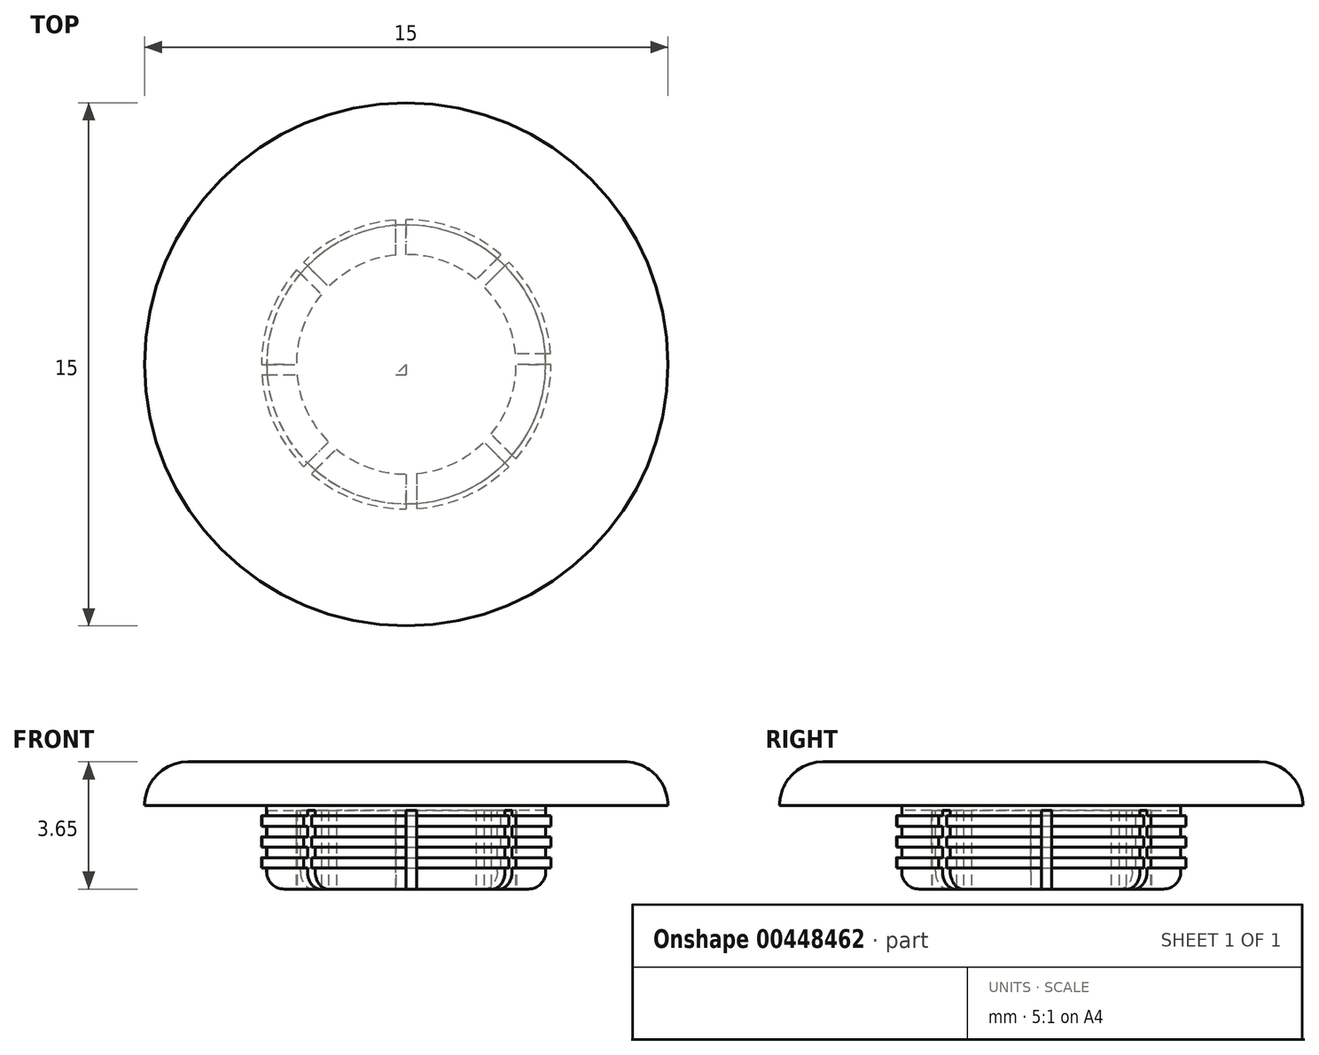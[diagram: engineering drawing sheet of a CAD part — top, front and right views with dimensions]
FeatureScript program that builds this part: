
annotation { "Feature Type Name" : "Feature", "Feature Type Description" : "" }
export const myFeature = defineFeature(function(context is Context, id is Id, definition is map)
    precondition{}
    {
        {
            var Q0;
            Q0=qCreatedBy(makeId("Top.planeOp"),FACE);
            var sketch = newSketch(context, id + "F0", { "sketchPlane" : qUnion([Q0])});
            skCircle(sketch, "E0", {"center": v(0, 0) * mm, "radius": 7.5 * mm});
            skCircle(sketch, "E1", {"center": v(0, 0) * mm, "radius": 4 * mm});
            skCircle(sketch, "E2", {"center": v(0, 0) * mm, "radius": 3.15 * mm});
            skSolve(sketch);
        }
        {
            var Q0;
            Q0=makeQuery(id+"F0.imprint","IMPRINT",FACE,{"disambiguationData":[TD([[makeQuery(id+"F0.imprint","IMPRINT",EDGE,{"derivedFrom":sQuery(id+"F0.wireOp",EDGE,"E0")}),1.0]])]});
            var Q1;
            Q1=makeQuery(id+"F0.imprint","IMPRINT",FACE,{"disambiguationData":[TD([[makeQuery(id+"F0.imprint","IMPRINT",EDGE,{"derivedFrom":sQuery(id+"F0.wireOp",EDGE,"E1")}),1.0]])]});
            var Q2;
            Q2=makeQuery(id+"F0.imprint","IMPRINT",FACE,{"disambiguationData":[TD([[makeQuery(id+"F0.imprint","IMPRINT",EDGE,{"derivedFrom":sQuery(id+"F0.wireOp",EDGE,"E2")}),1.0]])]});
            extrude(context, id + "F1", {"entities" : qUnion([Q0, Q1, Q2]), "depth" : 1.25 * mm});
        }
        {
            var Q0;
            Q0=makeQuery(id+"F1.opExtrude","CAP_EDGE",EDGE,{"disambiguationData":[OSD([sQuery(id+"F0.wireOp",EDGE,"E0")])],"isStart":false});
            fillet(context, id + "F2", {"entities" : qUnion([Q0]), "radius" : 1.25 * mm, "tangentPropagation" : true, "allowEdgeOverflow" : false});
        }
        {
            var Q0;
            Q0=makeQuery(id+"F0.imprint","IMPRINT",FACE,{"disambiguationData":[TD([[makeQuery(id+"F0.imprint","IMPRINT",EDGE,{"derivedFrom":sQuery(id+"F0.wireOp",EDGE,"E1")}),1.0]])]});
            var Q1;
            Q1=makeQuery(id+"F0.imprint","IMPRINT",FACE,{"disambiguationData":[TD([[makeQuery(id+"F0.imprint","IMPRINT",EDGE,{"derivedFrom":sQuery(id+"F0.wireOp",EDGE,"E2")}),1.0]])]});
            extrude(context, id + "F3", {"entities" : qUnion([Q0, Q1]), "operationType" : NewBodyOperationType.ADD, "oppositeDirection" : true, "depth" : .3 * mm});
        }
        {
            var Q0;
            Q0=makeQuery(id+"F3.opExtrude","CAP_FACE",FACE,{"disambiguationData":[OSD([sQuery(id+"F0.wireOp",EDGE,"E1"),sQuery(id+"F0.wireOp",EDGE,"E2")])],"isStart":false});
            var sketch = newSketch(context, id + "F4", { "sketchPlane" : qUnion([Q0])});
            skCircle(sketch, "E3", {"center": v(0, 0) * mm, "radius": 4.15 * mm});
            skSolve(sketch);
        }
        {
            var Q0;
            Q0=makeQuery(id+"F4.imprint","IMPRINT",FACE,{"disambiguationData":[TD([[makeQuery(id+"F4.imprint","IMPRINT",EDGE,{"derivedFrom":sQuery(id+"F4.wireOp",EDGE,"E3")}),1.0]])]});
            var Q1;
            Q1=makeQuery(id+"F4.imprint","IMPRINT",FACE,{"disambiguationData":[TD([[makeQuery(id+"F4.imprint","IMPRINT",EDGE,{"derivedFrom":makeQuery(id+"F3.opExtrude","CAP_EDGE",EDGE,{"disambiguationData":[OSD([sQuery(id+"F0.wireOp",EDGE,"E1")])],"isStart":false})}),-1.0]])]});
            var Q2;
            Q2=makeQuery(id+"F4.imprint","IMPRINT",FACE,{"disambiguationData":[TD([[makeQuery(id+"F4.imprint","IMPRINT",EDGE,{"derivedFrom":makeQuery(id+"F3.opExtrude","CAP_EDGE",EDGE,{"disambiguationData":[OSD([sQuery(id+"F0.wireOp",EDGE,"E2")])],"isStart":false})}),-1.0]])]});
            extrude(context, id + "F5", {"entities" : qUnion([Q0, Q1, Q2]), "operationType" : NewBodyOperationType.ADD, "depth" : .3 * mm});
        }
        {
            var Q0;
            Q0=makeQuery(id+"F5.opExtrude","CAP_FACE",FACE,{"disambiguationData":[OSD([sQuery(id+"F4.wireOp",EDGE,"E3")])],"isStart":false});
            var sketch = newSketch(context, id + "F6", { "sketchPlane" : qUnion([Q0])});
            skCircle(sketch, "E4", {"center": v(0, 0) * mm, "radius": 4 * mm});
            skSolve(sketch);
        }
        {
            var Q0;
            Q0=qSketchRegion(id+"F6",true);
            extrude(context, id + "F7", {"entities" : qUnion([Q0]), "operationType" : NewBodyOperationType.ADD, "depth" : .3 * mm});
        }
        {
            var Q0;
            Q0=makeQuery(id+"F7.opExtrude","CAP_FACE",FACE,{"disambiguationData":[OSD([sQuery(id+"F6.wireOp",EDGE,"E4")])],"isStart":false});
            var sketch = newSketch(context, id + "F8", { "sketchPlane" : qUnion([Q0])});
            skCircle(sketch, "E5", {"center": v(0, 0) * mm, "radius": 4.15 * mm});
            skSolve(sketch);
        }
        {
            var Q0;
            Q0=qSketchRegion(id+"F8",true);
            extrude(context, id + "F9", {"entities" : qUnion([Q0]), "operationType" : NewBodyOperationType.ADD, "depth" : .3 * mm});
        }
        {
            var Q0;
            Q0=makeQuery(id+"F9.opExtrude","CAP_FACE",FACE,{"disambiguationData":[OSD([sQuery(id+"F8.wireOp",EDGE,"E5")])],"isStart":false});
            var sketch = newSketch(context, id + "F10", { "sketchPlane" : qUnion([Q0])});
            skCircle(sketch, "E6", {"center": v(0, 0) * mm, "radius": 4 * mm});
            skSolve(sketch);
        }
        {
            var Q0;
            Q0=qSketchRegion(id+"F10",true);
            extrude(context, id + "F11", {"entities" : qUnion([Q0]), "operationType" : NewBodyOperationType.ADD, "depth" : .3 * mm});
        }
        {
            var Q0;
            Q0=makeQuery(id+"F11.opExtrude","CAP_FACE",FACE,{"disambiguationData":[OSD([sQuery(id+"F10.wireOp",EDGE,"E6")])],"isStart":false});
            var sketch = newSketch(context, id + "F12", { "sketchPlane" : qUnion([Q0])});
            skCircle(sketch, "E7", {"center": v(0, 0) * mm, "radius": 4.15 * mm});
            skSolve(sketch);
        }
        {
            var Q0;
            Q0=qSketchRegion(id+"F12",true);
            extrude(context, id + "F13", {"entities" : qUnion([Q0]), "operationType" : NewBodyOperationType.ADD, "depth" : .3 * mm});
        }
        {
            var Q0;
            Q0=makeQuery(id+"F13.opExtrude","CAP_FACE",FACE,{"disambiguationData":[OSD([sQuery(id+"F12.wireOp",EDGE,"E7")])],"isStart":false});
            var sketch = newSketch(context, id + "F14", { "sketchPlane" : qUnion([Q0])});
            skCircle(sketch, "E8", {"center": v(0, 0) * mm, "radius": 4 * mm});
            skSolve(sketch);
        }
        {
            var Q0;
            Q0=qSketchRegion(id+"F14",true);
            extrude(context, id + "F15", {"entities" : qUnion([Q0]), "operationType" : NewBodyOperationType.ADD, "depth" : .6 * mm});
        }
        {
            var Q0;
            Q0=makeQuery(id+"F15.opExtrude","CAP_FACE",FACE,{"disambiguationData":[OSD([sQuery(id+"F14.wireOp",EDGE,"E8")])],"isStart":false});
            fillet(context, id + "F16", {"entities" : qUnion([Q0]), "radius" : .5 * mm, "tangentPropagation" : true, "allowEdgeOverflow" : false});
        }
        {
            var Q0;
            Q0=makeQuery(id+"F15.opExtrude","CAP_FACE",FACE,{"disambiguationData":[OSD([sQuery(id+"F14.wireOp",EDGE,"E8")])],"isStart":false});
            var sketch = newSketch(context, id + "F17", { "sketchPlane" : qUnion([Q0])});
            skCircle(sketch, "E9", {"center": v(0, 0) * mm, "radius": 3.15 * mm});
            skLineSegment(sketch, "E10", {"start": v(0, 0) * mm, "end": v(0, 6) * mm});
            skLineSegment(sketch, "E11", {"start": v(0, 0) * mm, "end": v(-4.24, 4.24) * mm});
            skLineSegment(sketch, "E12", {"start": v(-4.24, 4.24) * mm, "end": v(0, 0) * mm});
            skLineSegment(sketch, "E13", {"start": v(-6, 0) * mm, "end": v(0, 0) * mm});
            skLineSegment(sketch, "E14.MirrorCS", {"start": v(0, 0) * mm, "end": v(0, -6) * mm});
            skLineSegment(sketch, "E15.MirrorCS", {"start": v(-4.24, -4.24) * mm, "end": v(0, 0) * mm});
            skLineSegment(sketch, "E16.MirrorCS", {"start": v(4.24, 4.24) * mm, "end": v(0, 0) * mm});
            skLineSegment(sketch, "E17.MirrorCS", {"start": v(6, 0) * mm, "end": v(0, 0) * mm});
            skLineSegment(sketch, "E18.MirrorCS", {"start": v(4.24, -4.24) * mm, "end": v(0, 0) * mm});
            skLineSegment(sketch, "E19.0", {"start": v(0.3, 0) * mm, "end": v(0.3, 6) * mm});
            skLineSegment(sketch, "E20.0", {"start": v(6, -0.3) * mm, "end": v(0, -0.3) * mm});
            skLineSegment(sketch, "E21.0", {"start": v(4.03, -4.45) * mm, "end": v(-0.21, -0.21) * mm});
            skLineSegment(sketch, "E22.0", {"start": v(-0.3, 0) * mm, "end": v(-0.3, -6) * mm});
            skLineSegment(sketch, "E23.0", {"start": v(-4.45, -4.03) * mm, "end": v(-0.21, 0.21) * mm});
            skLineSegment(sketch, "E24.0", {"start": v(-6, 0.3) * mm, "end": v(0, 0.3) * mm});
            skLineSegment(sketch, "E25.0", {"start": v(-4.03, 4.45) * mm, "end": v(0.21, 0.21) * mm});
            skLineSegment(sketch, "E26.0", {"start": v(4.45, 4.03) * mm, "end": v(0.21, -0.21) * mm});
            skLineSegment(sketch, "E27", {"start": v(-4.24, 4.24) * mm, "end": v(-4.03, 4.45) * mm});
            skLineSegment(sketch, "E28", {"start": v(0, 6) * mm, "end": v(0.3, 6) * mm});
            skLineSegment(sketch, "E29", {"start": v(4.24, 4.24) * mm, "end": v(4.45, 4.03) * mm});
            skLineSegment(sketch, "E30", {"start": v(6, 0) * mm, "end": v(6, -0.3) * mm});
            skLineSegment(sketch, "E31", {"start": v(4.24, -4.24) * mm, "end": v(4.03, -4.45) * mm});
            skLineSegment(sketch, "E32", {"start": v(0, -6) * mm, "end": v(-0.3, -6) * mm});
            skLineSegment(sketch, "E33", {"start": v(-4.24, -4.24) * mm, "end": v(-4.45, -4.03) * mm});
            skLineSegment(sketch, "E34", {"start": v(-6, 0) * mm, "end": v(-6, 0.3) * mm});
            skSolve(sketch);
        }
        {
            var Q0;
            Q0=makeQuery(id+"F17.imprint","IMPRINT",FACE,{"disambiguationData":[TD([[makeQuery(id+"F17.imprint","IMPRINT",EDGE,{"derivedFrom":sQuery(id+"F17.wireOp",EDGE,"E9")}),1.0]])]});
            var Q1;
            {var subQ1=sQuery(id+"F17.wireOp",EDGE,"E9");var subQ7=sQuery(id+"F17.wireOp",EDGE,"E25.0");var subQ9=makeQuery(id+"F17.imprint","INTERSECT",VERTEX,{"derivedFrom":[subQ1,subQ7]});Q1=makeQuery(id+"F17.imprint","IMPRINT",FACE,{"disambiguationData":[TD([[makeQuery(id+"F17.imprint","IMPRINT",EDGE,{"disambiguationData":[TD([[subQ9,-1.0]])],"derivedFrom":subQ1}),1.0]])]});}
            var Q2;
            {var subQ0=sQuery(id+"F17.wireOp",EDGE,"E19.0");var subQ1=sQuery(id+"F17.wireOp",EDGE,"E9");var subQ2=makeQuery(id+"F17.imprint","INTERSECT",VERTEX,{"derivedFrom":[subQ1,subQ0]});Q2=makeQuery(id+"F17.imprint","IMPRINT",FACE,{"disambiguationData":[TD([[makeQuery(id+"F17.imprint","IMPRINT",EDGE,{"disambiguationData":[TD([[subQ2,-1.0]])],"derivedFrom":subQ1}),1.0]])]});}
            var Q3;
            {var subQ5=sQuery(id+"F17.wireOp",EDGE,"E9");var subQ7=sQuery(id+"F17.wireOp",EDGE,"E26.0");var subQ8=makeQuery(id+"F17.imprint","INTERSECT",VERTEX,{"derivedFrom":[subQ5,subQ7]});Q3=makeQuery(id+"F17.imprint","IMPRINT",FACE,{"disambiguationData":[TD([[makeQuery(id+"F17.imprint","IMPRINT",EDGE,{"disambiguationData":[TD([[subQ8,-1.0]])],"derivedFrom":subQ5}),1.0]])]});}
            var Q4;
            {var subQ1=sQuery(id+"F17.wireOp",EDGE,"E9");var subQ5=sQuery(id+"F17.wireOp",EDGE,"E17.MirrorCS");var subQ6=makeQuery(id+"F17.imprint","INTERSECT",VERTEX,{"derivedFrom":[subQ1,subQ5]});Q4=makeQuery(id+"F17.imprint","IMPRINT",FACE,{"disambiguationData":[TD([[makeQuery(id+"F17.imprint","IMPRINT",EDGE,{"disambiguationData":[TD([[subQ6,1.0]])],"derivedFrom":subQ1}),1.0]])]});}
            var Q5;
            {var subQ1=sQuery(id+"F17.wireOp",EDGE,"E9");var subQ7=sQuery(id+"F17.wireOp",EDGE,"E21.0");var subQ9=makeQuery(id+"F17.imprint","INTERSECT",VERTEX,{"derivedFrom":[subQ1,subQ7]});Q5=makeQuery(id+"F17.imprint","IMPRINT",FACE,{"disambiguationData":[TD([[makeQuery(id+"F17.imprint","IMPRINT",EDGE,{"disambiguationData":[TD([[subQ9,-1.0]])],"derivedFrom":subQ1}),1.0]])]});}
            var Q6;
            {var subQ3=sQuery(id+"F17.wireOp",EDGE,"E22.0");var subQ7=sQuery(id+"F17.wireOp",EDGE,"E9");var subQ9=makeQuery(id+"F17.imprint","INTERSECT",VERTEX,{"derivedFrom":[subQ7,subQ3]});Q6=makeQuery(id+"F17.imprint","IMPRINT",FACE,{"disambiguationData":[TD([[makeQuery(id+"F17.imprint","IMPRINT",EDGE,{"disambiguationData":[TD([[subQ9,-1.0]])],"derivedFrom":subQ7}),1.0]])]});}
            var Q7;
            {var subQ5=sQuery(id+"F17.wireOp",EDGE,"E9");var subQ7=sQuery(id+"F17.wireOp",EDGE,"E23.0");var subQ9=makeQuery(id+"F17.imprint","INTERSECT",VERTEX,{"derivedFrom":[subQ5,subQ7]});Q7=makeQuery(id+"F17.imprint","IMPRINT",FACE,{"disambiguationData":[TD([[makeQuery(id+"F17.imprint","IMPRINT",EDGE,{"disambiguationData":[TD([[subQ9,-1.0]])],"derivedFrom":subQ5}),1.0]])]});}
            var Q8;
            {var subQ1=sQuery(id+"F17.wireOp",EDGE,"E9");var subQ7=sQuery(id+"F17.wireOp",EDGE,"E24.0");var subQ8=makeQuery(id+"F17.imprint","INTERSECT",VERTEX,{"derivedFrom":[subQ1,subQ7]});Q8=makeQuery(id+"F17.imprint","IMPRINT",FACE,{"disambiguationData":[TD([[makeQuery(id+"F17.imprint","IMPRINT",EDGE,{"disambiguationData":[TD([[subQ8,-1.0]])],"derivedFrom":subQ1}),1.0]])]});}
            var Q9;
            {var subQ0=sQuery(id+"F17.wireOp",EDGE,"E17.MirrorCS");var subQ1=makeQuery(id+"F17.imprint","INTERSECT",VERTEX,{"derivedFrom":[subQ0,sQuery(id+"F17.wireOp",EDGE,"E19.0")]});Q9=makeQuery(id+"F17.imprint","IMPRINT",FACE,{"disambiguationData":[TD([[makeQuery(id+"F17.imprint","IMPRINT",EDGE,{"disambiguationData":[TD([[subQ1,1.0]])],"derivedFrom":subQ0}),1.0]])]});}
            var Q10;
            {var subQ0=sQuery(id+"F17.wireOp",EDGE,"E16.MirrorCS");var subQ1=makeQuery(id+"F17.imprint","INTERSECT",VERTEX,{"derivedFrom":[subQ0,sQuery(id+"F17.wireOp",EDGE,"E25.0")]});Q10=makeQuery(id+"F17.imprint","IMPRINT",FACE,{"disambiguationData":[TD([[makeQuery(id+"F17.imprint","IMPRINT",EDGE,{"disambiguationData":[TD([[subQ1,1.0]])],"derivedFrom":subQ0}),1.0]])]});}
            var Q11;
            {var subQ1=sQuery(id+"F17.wireOp",EDGE,"E10");var subQ3=makeQuery(id+"F17.imprint","INTERSECT",VERTEX,{"derivedFrom":[subQ1,sQuery(id+"F17.wireOp",EDGE,"E24.0")]});Q11=makeQuery(id+"F17.imprint","IMPRINT",FACE,{"disambiguationData":[TD([[makeQuery(id+"F17.imprint","IMPRINT",EDGE,{"disambiguationData":[TD([[subQ3,-1.0]])],"derivedFrom":subQ1}),-1.0]])]});}
            var Q12;
            {var subQ0=sQuery(id+"F17.wireOp",EDGE,"E12");var subQ5=makeQuery(id+"F17.imprint","INTERSECT",VERTEX,{"derivedFrom":[subQ0,sQuery(id+"F17.wireOp",EDGE,"E23.0")]});Q12=makeQuery(id+"F17.imprint","IMPRINT",FACE,{"disambiguationData":[TD([[makeQuery(id+"F17.imprint","IMPRINT",EDGE,{"disambiguationData":[TD([[subQ5,1.0]])],"derivedFrom":subQ0}),1.0]])]});}
            var Q13;
            {var subQ0=sQuery(id+"F17.wireOp",EDGE,"E13");var subQ5=makeQuery(id+"F17.imprint","INTERSECT",VERTEX,{"derivedFrom":[subQ0,sQuery(id+"F17.wireOp",EDGE,"E22.0")]});Q13=makeQuery(id+"F17.imprint","IMPRINT",FACE,{"disambiguationData":[TD([[makeQuery(id+"F17.imprint","IMPRINT",EDGE,{"disambiguationData":[TD([[subQ5,1.0]])],"derivedFrom":subQ0}),1.0]])]});}
            var Q14;
            {var subQ0=sQuery(id+"F17.wireOp",EDGE,"E15.MirrorCS");var subQ6=makeQuery(id+"F17.imprint","INTERSECT",VERTEX,{"derivedFrom":[subQ0,sQuery(id+"F17.wireOp",EDGE,"E21.0")]});Q14=makeQuery(id+"F17.imprint","IMPRINT",FACE,{"disambiguationData":[TD([[makeQuery(id+"F17.imprint","IMPRINT",EDGE,{"disambiguationData":[TD([[subQ6,1.0]])],"derivedFrom":subQ0}),1.0]])]});}
            var Q15;
            {var subQ1=sQuery(id+"F17.wireOp",EDGE,"E14.MirrorCS");var subQ3=makeQuery(id+"F17.imprint","INTERSECT",VERTEX,{"derivedFrom":[subQ1,sQuery(id+"F17.wireOp",EDGE,"E20.0")]});Q15=makeQuery(id+"F17.imprint","IMPRINT",FACE,{"disambiguationData":[TD([[makeQuery(id+"F17.imprint","IMPRINT",EDGE,{"disambiguationData":[TD([[subQ3,-1.0]])],"derivedFrom":subQ1}),-1.0]])]});}
            var Q16;
            {var subQ0=sQuery(id+"F17.wireOp",EDGE,"E18.MirrorCS");var subQ6=makeQuery(id+"F17.imprint","INTERSECT",VERTEX,{"derivedFrom":[subQ0,sQuery(id+"F17.wireOp",EDGE,"E26.0")]});Q16=makeQuery(id+"F17.imprint","IMPRINT",FACE,{"disambiguationData":[TD([[makeQuery(id+"F17.imprint","IMPRINT",EDGE,{"disambiguationData":[TD([[subQ6,1.0]])],"derivedFrom":subQ0}),1.0]])]});}
            var Q17;
            {var subQ0=sQuery(id+"F17.wireOp",EDGE,"E27");Q17=makeQuery(id+"F17.imprint","IMPRINT",FACE,{"disambiguationData":[TD([[makeQuery(id+"F17.imprint","IMPRINT",EDGE,{"derivedFrom":subQ0}),-1.0]])]});}
            var Q18;
            {var subQ0=sQuery(id+"F17.wireOp",EDGE,"E25.0");var subQ1=sQuery(id+"F17.wireOp",EDGE,"E9");var subQ2=makeQuery(id+"F17.imprint","INTERSECT",VERTEX,{"derivedFrom":[subQ1,subQ0]});Q18=makeQuery(id+"F17.imprint","IMPRINT",FACE,{"disambiguationData":[TD([[makeQuery(id+"F17.imprint","IMPRINT",EDGE,{"disambiguationData":[TD([[subQ2,-1.0]])],"derivedFrom":subQ1}),-1.0]])]});}
            var Q19;
            {var subQ0=sQuery(id+"F17.wireOp",EDGE,"E34");Q19=makeQuery(id+"F17.imprint","IMPRINT",FACE,{"disambiguationData":[TD([[makeQuery(id+"F17.imprint","IMPRINT",EDGE,{"derivedFrom":subQ0}),-1.0]])]});}
            var Q20;
            {var subQ0=sQuery(id+"F17.wireOp",EDGE,"E24.0");var subQ1=sQuery(id+"F17.wireOp",EDGE,"E9");var subQ2=makeQuery(id+"F17.imprint","INTERSECT",VERTEX,{"derivedFrom":[subQ1,subQ0]});Q20=makeQuery(id+"F17.imprint","IMPRINT",FACE,{"disambiguationData":[TD([[makeQuery(id+"F17.imprint","IMPRINT",EDGE,{"disambiguationData":[TD([[subQ2,-1.0]])],"derivedFrom":subQ1}),-1.0]])]});}
            var Q21;
            {var subQ0=sQuery(id+"F17.wireOp",EDGE,"E33");Q21=makeQuery(id+"F17.imprint","IMPRINT",FACE,{"disambiguationData":[TD([[makeQuery(id+"F17.imprint","IMPRINT",EDGE,{"derivedFrom":subQ0}),-1.0]])]});}
            var Q22;
            {var subQ0=sQuery(id+"F17.wireOp",EDGE,"E23.0");var subQ1=sQuery(id+"F17.wireOp",EDGE,"E9");var subQ2=makeQuery(id+"F17.imprint","INTERSECT",VERTEX,{"derivedFrom":[subQ1,subQ0]});Q22=makeQuery(id+"F17.imprint","IMPRINT",FACE,{"disambiguationData":[TD([[makeQuery(id+"F17.imprint","IMPRINT",EDGE,{"disambiguationData":[TD([[subQ2,-1.0]])],"derivedFrom":subQ1}),-1.0]])]});}
            var Q23;
            {var subQ0=sQuery(id+"F17.wireOp",EDGE,"E32");Q23=makeQuery(id+"F17.imprint","IMPRINT",FACE,{"disambiguationData":[TD([[makeQuery(id+"F17.imprint","IMPRINT",EDGE,{"derivedFrom":subQ0}),-1.0]])]});}
            var Q24;
            {var subQ0=sQuery(id+"F17.wireOp",EDGE,"E22.0");var subQ1=sQuery(id+"F17.wireOp",EDGE,"E9");var subQ2=makeQuery(id+"F17.imprint","INTERSECT",VERTEX,{"derivedFrom":[subQ1,subQ0]});Q24=makeQuery(id+"F17.imprint","IMPRINT",FACE,{"disambiguationData":[TD([[makeQuery(id+"F17.imprint","IMPRINT",EDGE,{"disambiguationData":[TD([[subQ2,-1.0]])],"derivedFrom":subQ1}),-1.0]])]});}
            var Q25;
            {var subQ0=sQuery(id+"F17.wireOp",EDGE,"E31");Q25=makeQuery(id+"F17.imprint","IMPRINT",FACE,{"disambiguationData":[TD([[makeQuery(id+"F17.imprint","IMPRINT",EDGE,{"derivedFrom":subQ0}),-1.0]])]});}
            var Q26;
            {var subQ0=sQuery(id+"F17.wireOp",EDGE,"E21.0");var subQ1=sQuery(id+"F17.wireOp",EDGE,"E9");var subQ2=makeQuery(id+"F17.imprint","INTERSECT",VERTEX,{"derivedFrom":[subQ1,subQ0]});Q26=makeQuery(id+"F17.imprint","IMPRINT",FACE,{"disambiguationData":[TD([[makeQuery(id+"F17.imprint","IMPRINT",EDGE,{"disambiguationData":[TD([[subQ2,-1.0]])],"derivedFrom":subQ1}),-1.0]])]});}
            var Q27;
            {var subQ0=sQuery(id+"F17.wireOp",EDGE,"E30");Q27=makeQuery(id+"F17.imprint","IMPRINT",FACE,{"disambiguationData":[TD([[makeQuery(id+"F17.imprint","IMPRINT",EDGE,{"derivedFrom":subQ0}),-1.0]])]});}
            var Q28;
            {var subQ0=sQuery(id+"F17.wireOp",EDGE,"E17.MirrorCS");var subQ1=sQuery(id+"F17.wireOp",EDGE,"E9");var subQ2=makeQuery(id+"F17.imprint","INTERSECT",VERTEX,{"derivedFrom":[subQ1,subQ0]});Q28=makeQuery(id+"F17.imprint","IMPRINT",FACE,{"disambiguationData":[TD([[makeQuery(id+"F17.imprint","IMPRINT",EDGE,{"disambiguationData":[TD([[subQ2,1.0]])],"derivedFrom":subQ1}),-1.0]])]});}
            var Q29;
            {var subQ0=sQuery(id+"F17.wireOp",EDGE,"E29");Q29=makeQuery(id+"F17.imprint","IMPRINT",FACE,{"disambiguationData":[TD([[makeQuery(id+"F17.imprint","IMPRINT",EDGE,{"derivedFrom":subQ0}),-1.0]])]});}
            var Q30;
            {var subQ0=sQuery(id+"F17.wireOp",EDGE,"E26.0");var subQ1=sQuery(id+"F17.wireOp",EDGE,"E9");var subQ2=makeQuery(id+"F17.imprint","INTERSECT",VERTEX,{"derivedFrom":[subQ1,subQ0]});Q30=makeQuery(id+"F17.imprint","IMPRINT",FACE,{"disambiguationData":[TD([[makeQuery(id+"F17.imprint","IMPRINT",EDGE,{"disambiguationData":[TD([[subQ2,-1.0]])],"derivedFrom":subQ1}),-1.0]])]});}
            var Q31;
            {var subQ0=sQuery(id+"F17.wireOp",EDGE,"E28");Q31=makeQuery(id+"F17.imprint","IMPRINT",FACE,{"disambiguationData":[TD([[makeQuery(id+"F17.imprint","IMPRINT",EDGE,{"derivedFrom":subQ0}),-1.0]])]});}
            var Q32;
            {var subQ0=sQuery(id+"F17.wireOp",EDGE,"E19.0");var subQ1=sQuery(id+"F17.wireOp",EDGE,"E9");var subQ2=makeQuery(id+"F17.imprint","INTERSECT",VERTEX,{"derivedFrom":[subQ1,subQ0]});Q32=makeQuery(id+"F17.imprint","IMPRINT",FACE,{"disambiguationData":[TD([[makeQuery(id+"F17.imprint","IMPRINT",EDGE,{"disambiguationData":[TD([[subQ2,-1.0]])],"derivedFrom":subQ1}),-1.0]])]});}
            extrude(context, id + "F18", {"entities" : qUnion([Q0, Q1, Q2, Q3, Q4, Q5, Q6, Q7, Q8, Q9, Q10, Q11, Q12, Q13, Q14, Q15, Q16, Q17, Q18, Q19, Q20, Q21, Q22, Q23, Q24, Q25, Q26, Q27, Q28, Q29, Q30, Q31, Q32]), "operationType" : NewBodyOperationType.REMOVE, "oppositeDirection" : true, "depth" : 2.25 * mm});
        }
    });
